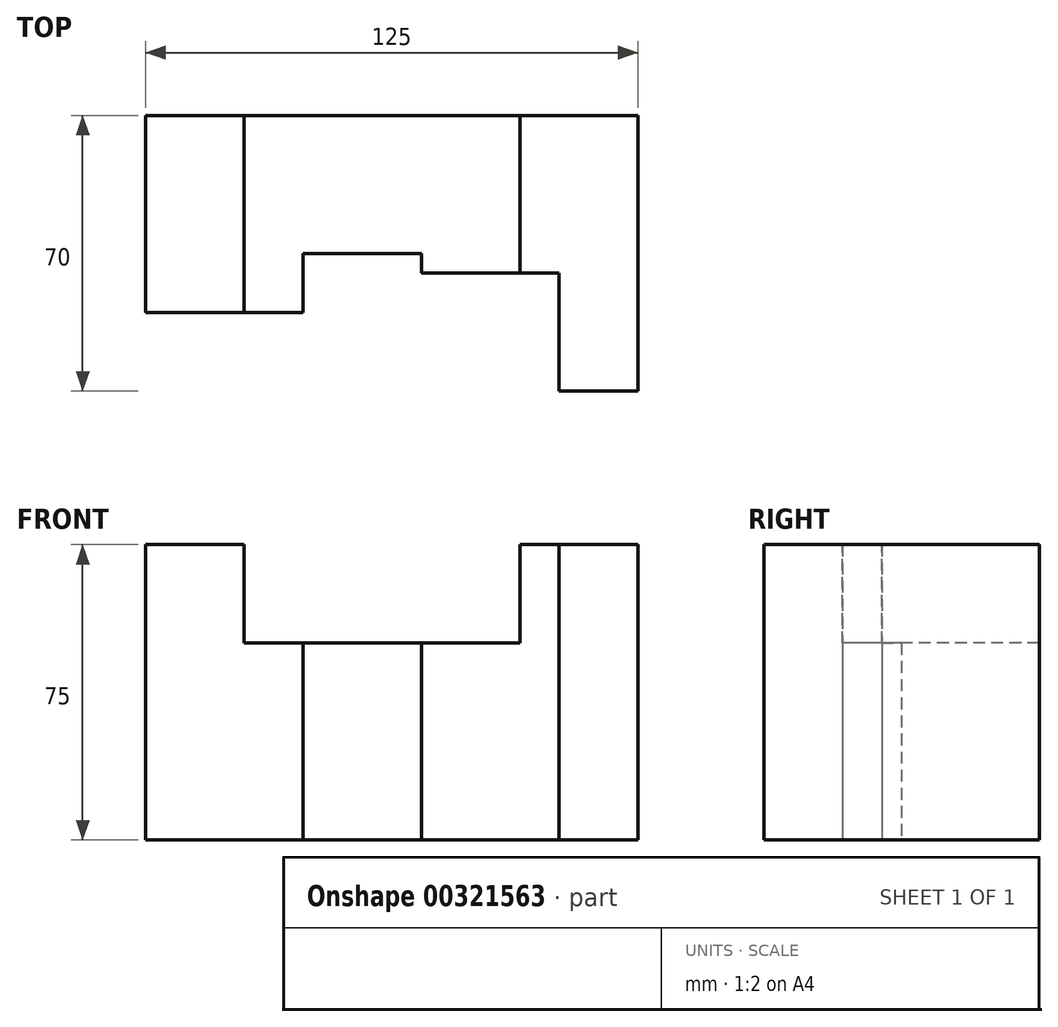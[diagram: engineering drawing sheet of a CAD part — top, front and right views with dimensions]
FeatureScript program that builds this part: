
annotation { "Feature Type Name" : "Feature", "Feature Type Description" : "" }
export const myFeature = defineFeature(function(context is Context, id is Id, definition is map)
    precondition{}
    {
        {
            var Q0;
            Q0=qCreatedBy(makeId("Front.planeOp"),FACE);
            var sketch = newSketch(context, id + "F0", { "sketchPlane" : qUnion([Q0])});
            skLineSegment(sketch, "E0.bottom", {"start": v(0, 0) * mm, "end": v(125, 0) * mm});
            skLineSegment(sketch, "E0.top", {"start": v(0, 75) * mm, "end": v(125, 75) * mm});
            skLineSegment(sketch, "E0.left", {"start": v(0, 0) * mm, "end": v(0, 75) * mm});
            skLineSegment(sketch, "E0.right", {"start": v(125, 0) * mm, "end": v(125, 75) * mm});
            skSolve(sketch);
        }
        {
            var Q0;
            Q0 = qSketchRegion(id + "F0", true);
            extrude(context, id + "F1", {"entities" : qUnion([Q0]), "oppositeDirection" : true, "depth" : 70 * mm});
        }
        {
            var Q0;
            Q0=makeQuery(id+"F1.opExtrude","CAP_FACE",FACE,{"disambiguationData":[OSD([sQuery(id+"F0.wireOp",EDGE,"E0.bottom"),sQuery(id+"F0.wireOp",EDGE,"E0.top"),sQuery(id+"F0.wireOp",EDGE,"E0.left"),sQuery(id+"F0.wireOp",EDGE,"E0.right")])],"isStart":true});
            var sketch = newSketch(context, id + "F2", { "sketchPlane" : qUnion([Q0])});
            skLineSegment(sketch, "E1.bottom", {"start": v(25, 75) * mm, "end": v(95, 75) * mm});
            skLineSegment(sketch, "E1.top", {"start": v(25, 50) * mm, "end": v(95, 50) * mm});
            skLineSegment(sketch, "E1.left", {"start": v(25, 75) * mm, "end": v(25, 50) * mm});
            skLineSegment(sketch, "E1.right", {"start": v(95, 75) * mm, "end": v(95, 50) * mm});
            skSolve(sketch);
        }
        {
            var Q0;
            Q0 = qSketchRegion(id + "F2", true);
            extrude(context, id + "F3", {"entities" : qUnion([Q0]), "operationType" : NewBodyOperationType.REMOVE, "endBound" : BoundingType.THROUGH_ALL, "oppositeDirection" : true, "depth" : 25 * mm});
        }
        {
            var Q0;
            Q0=qCreatedBy(makeId("Top.planeOp"),FACE);
            var sketch = newSketch(context, id + "F4", { "sketchPlane" : qUnion([Q0])});
            skLineSegment(sketch, "E2", {"start": v(105, 30) * mm, "end": v(70, 30) * mm});
            skLineSegment(sketch, "E3", {"start": v(70, 30) * mm, "end": v(70, 35) * mm});
            skLineSegment(sketch, "E4", {"start": v(70, 35) * mm, "end": v(40, 35) * mm});
            skLineSegment(sketch, "E5", {"start": v(40, 35) * mm, "end": v(40, 20) * mm});
            skLineSegment(sketch, "E6", {"start": v(40, 20) * mm, "end": v(0, 20) * mm});
            skLineSegment(sketch, "E7", {"start": v(0, 20) * mm, "end": v(0, -31.13) * mm});
            skLineSegment(sketch, "E8", {"start": v(0, -31.13) * mm, "end": v(125, -31.13) * mm});
            skPoint(sketch, "E9.end.orphan", {"position": v(125, 0) * mm});
            skLineSegment(sketch, "E10", {"start": v(105, 30) * mm, "end": v(105, 0) * mm});
            skLineSegment(sketch, "E11", {"start": v(105, 0) * mm, "end": v(125, 0) * mm});
            skLineSegment(sketch, "E12", {"start": v(125, -31.13) * mm, "end": v(125, 0) * mm});
            skSolve(sketch);
        }
        {
            var Q0;
            Q0 = qSketchRegion(id + "F4", true);
            extrude(context, id + "F5", {"entities" : qUnion([Q0]), "operationType" : NewBodyOperationType.REMOVE, "endBound" : BoundingType.THROUGH_ALL, "depth" : 25 * mm});
        }
    });
